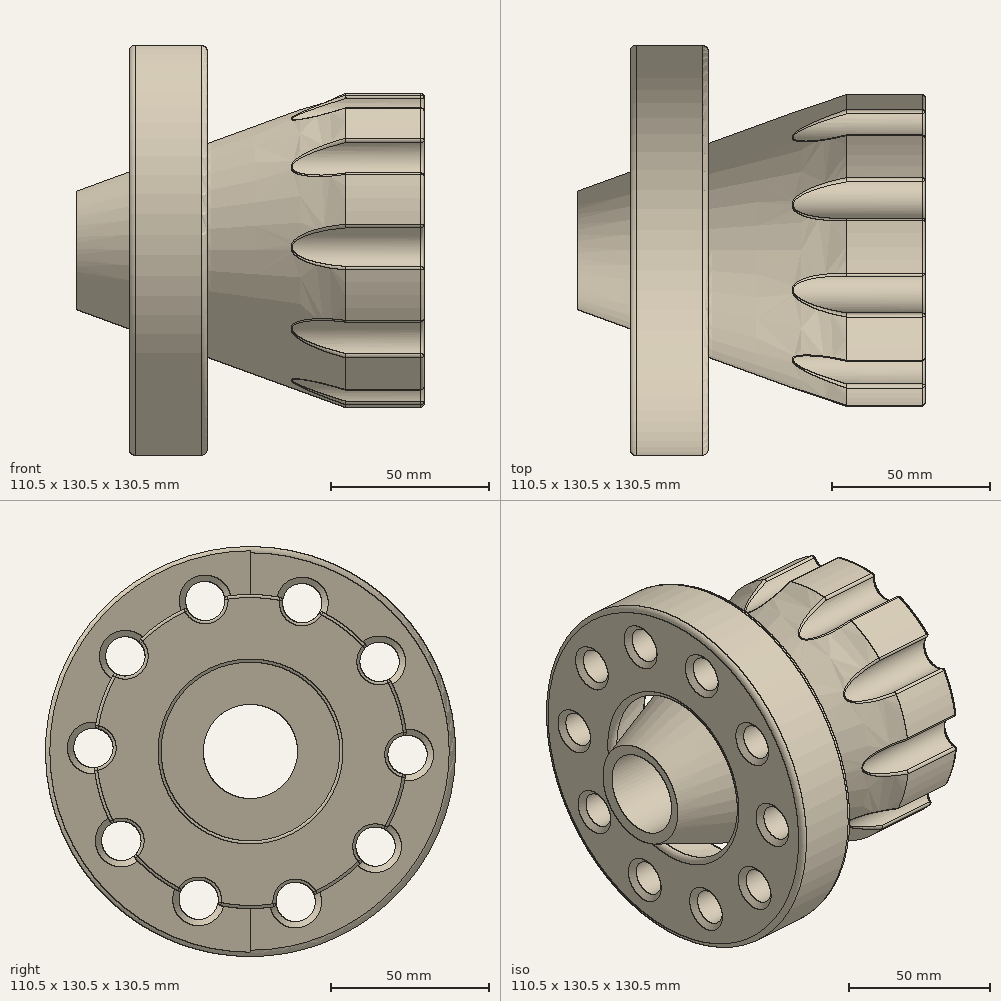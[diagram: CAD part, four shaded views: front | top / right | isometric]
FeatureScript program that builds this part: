
annotation { "Feature Type Name" : "Feature", "Feature Type Description" : "" }
export const myFeature = defineFeature(function(context is Context, id is Id, definition is map)
    precondition{}
    {
        {
            var Q0;
            Q0 = qCreatedBy(makeId("Front.planeOp"), FACE);
            var sketch = newSketch(context, id + "F0", { "sketchPlane" : qUnion([Q0])});
            skLineSegment(sketch, "E0", {"start": v(-83.1, 0) * mm, "end": v(0, 0) * mm, "construction": true});
            skLineSegment(sketch, "E1.bottom", {"start": v(25, 39.34) * mm, "end": v(0, 30.24) * mm});
            skLineSegment(sketch, "E1.top", {"start": v(25, 65.24) * mm, "end": v(0, 65.24) * mm});
            skLineSegment(sketch, "E1.left", {"start": v(25, 39.34) * mm, "end": v(25, 65.24) * mm});
            skLineSegment(sketch, "E1.right", {"start": v(0, 30.24) * mm, "end": v(0, 65.24) * mm});
            skLineSegment(sketch, "E2.0", {"start": v(68.9, 50) * mm, "end": v(-27.26, 15) * mm});
            skLineSegment(sketch, "E3", {"start": v(68.9, 50) * mm, "end": v(68.9, 15) * mm});
            skLineSegment(sketch, "E4", {"start": v(68.9, 15) * mm, "end": v(-27.26, 15) * mm});
            skPoint(sketch, "E5", {"position": v(-68.47, 0) * mm});
            skLineSegment(sketch, "E6", {"start": v(0, 0) * mm, "end": v(-68.47, 0) * mm});
            skSolve(sketch);
        }
        {
            var Q0;
            Q0=makeQuery(id+"F0.imprint","IMPRINT",FACE,{"disambiguationData":[TD([[makeQuery(id+"F0.imprint","IMPRINT",EDGE,{"derivedFrom":sQuery(id+"F0.wireOp",EDGE,"E2.0")}),1.0]])]});
            var Q1;
            Q1=sQuery(id+"F0.wireOp",EDGE,"E0");
            revolve(context, id + "F1", {"entities" : qUnion([Q0]), "axis" : qUnion([Q1]), "revolveType" : RevolveType.FULL});
        }
        {
            var Q0;
            Q0=makeQuery(id+"F1.opRevolve","SWEPT_FACE",FACE,{"disambiguationData":[OSD([sQuery(id+"F0.wireOp",EDGE,"E3")])]});
            var sketch = newSketch(context, id + "F2", { "sketchPlane" : qUnion([Q0])});
            skCircle(sketch, "E7", {"center": v(-49.99, 1.1) * mm, "radius": 6.26 * mm});
            skSolve(sketch);
        }
        {
            var Q0;
            {var subQ0=makeQuery(id+"F1.opRevolve","SWEPT_EDGE",EDGE,{"disambiguationData":[OSD([sQuery(id+"F0.wireOp",EDGE,"E2.0"),sQuery(id+"F0.wireOp",EDGE,"E3")])]});var subQ1=sQuery(id+"F2.wireOp",EDGE,"E7");var subQ3=makeQuery(id+"F2.imprint","INTERSECT",VERTEX,{"disambiguationData":[OD(0.0)],"derivedFrom":[subQ0,subQ1]});Q0=qUnion([makeQuery(id+"F2.imprint","IMPRINT",FACE,{"disambiguationData":[TD([[makeQuery(id+"F2.imprint","IMPRINT",EDGE,{"disambiguationData":[TD([[subQ3,1.0]])],"derivedFrom":subQ1}),1.0]])]}),makeQuery(id+"F2.imprint","IMPRINT",FACE,{"disambiguationData":[TD([[makeQuery(id+"F2.imprint","IMPRINT",EDGE,{"disambiguationData":[TD([[subQ3,-1.0]])],"derivedFrom":subQ1}),1.0]])]})]);}
            extrude(context, id + "F3", {"entities" : qUnion([Q0]), "oppositeDirection" : true, "depth" : 131.33 * mm});
        }
        {
            var Q0;
            Q0=makeQuery(id+"F3.opExtrude","SWEPT_BODY",BODY,{"disambiguationData":[OSD([sQuery(id+"F2.wireOp",EDGE,"E7")])]});
            var Q1;
            Q1=makeQuery(id+"F1.opRevolve","SWEPT_FACE",FACE,{"disambiguationData":[OSD([sQuery(id+"F0.wireOp",EDGE,"E4")])]});
            circularPattern(context, id + "F4", {"entities" : qUnion([Q0]), "axis" : qUnion([Q1]), "angle" : 360 * degree, "instanceCount" : 10, "equalSpace" : true});
        }
        {
            var Q0;
            Q0=makeQuery(id+"F0.imprint","IMPRINT",FACE,{"disambiguationData":[TD([[makeQuery(id+"F0.imprint","IMPRINT",EDGE,{"derivedFrom":sQuery(id+"F0.wireOp",EDGE,"E1.bottom")}),-1.0]])]});
            var Q1;
            Q1=sQuery(id+"F0.wireOp",EDGE,"E0");
            revolve(context, id + "F5", {"entities" : qUnion([Q0]), "axis" : qUnion([Q1]), "revolveType" : RevolveType.FULL});
        }
        {
            var Q0;
            Q0=makeQuery(id+"F4.opPattern","COPY",BODY,{"derivedFrom":makeQuery(id+"F3.opExtrude","SWEPT_BODY",BODY,{"disambiguationData":[OSD([sQuery(id+"F2.wireOp",EDGE,"E7")])]}),"instanceName":"4"});
            var Q1;
            Q1=makeQuery(id+"F4.opPattern","COPY",BODY,{"derivedFrom":makeQuery(id+"F3.opExtrude","SWEPT_BODY",BODY,{"disambiguationData":[OSD([sQuery(id+"F2.wireOp",EDGE,"E7")])]}),"instanceName":"3"});
            var Q2;
            Q2=makeQuery(id+"F4.opPattern","COPY",BODY,{"derivedFrom":makeQuery(id+"F3.opExtrude","SWEPT_BODY",BODY,{"disambiguationData":[OSD([sQuery(id+"F2.wireOp",EDGE,"E7")])]}),"instanceName":"2"});
            var Q3;
            Q3=makeQuery(id+"F4.opPattern","COPY",BODY,{"derivedFrom":makeQuery(id+"F3.opExtrude","SWEPT_BODY",BODY,{"disambiguationData":[OSD([sQuery(id+"F2.wireOp",EDGE,"E7")])]}),"instanceName":"1"});
            var Q4;
            Q4=makeQuery(id+"F3.opExtrude","SWEPT_BODY",BODY,{"disambiguationData":[OSD([sQuery(id+"F2.wireOp",EDGE,"E7")])]});
            var Q5;
            Q5=makeQuery(id+"F4.opPattern","COPY",BODY,{"derivedFrom":makeQuery(id+"F3.opExtrude","SWEPT_BODY",BODY,{"disambiguationData":[OSD([sQuery(id+"F2.wireOp",EDGE,"E7")])]}),"instanceName":"9"});
            var Q6;
            Q6=makeQuery(id+"F4.opPattern","COPY",BODY,{"derivedFrom":makeQuery(id+"F3.opExtrude","SWEPT_BODY",BODY,{"disambiguationData":[OSD([sQuery(id+"F2.wireOp",EDGE,"E7")])]}),"instanceName":"8"});
            var Q7;
            Q7=makeQuery(id+"F4.opPattern","COPY",BODY,{"derivedFrom":makeQuery(id+"F3.opExtrude","SWEPT_BODY",BODY,{"disambiguationData":[OSD([sQuery(id+"F2.wireOp",EDGE,"E7")])]}),"instanceName":"7"});
            var Q8;
            Q8=makeQuery(id+"F4.opPattern","COPY",BODY,{"derivedFrom":makeQuery(id+"F3.opExtrude","SWEPT_BODY",BODY,{"disambiguationData":[OSD([sQuery(id+"F2.wireOp",EDGE,"E7")])]}),"instanceName":"6"});
            var Q9;
            Q9=makeQuery(id+"F4.opPattern","COPY",BODY,{"derivedFrom":makeQuery(id+"F3.opExtrude","SWEPT_BODY",BODY,{"disambiguationData":[OSD([sQuery(id+"F2.wireOp",EDGE,"E7")])]}),"instanceName":"5"});
            var Q10;
            Q10=makeQuery(id+"F1.opRevolve","SWEPT_BODY",BODY,{"disambiguationData":[OSD([sQuery(id+"F0.wireOp",EDGE,"E2.0"),sQuery(id+"F0.wireOp",EDGE,"E3"),sQuery(id+"F0.wireOp",EDGE,"E4")])]});
            var Q11;
            Q11=makeQuery(id+"F5.opRevolve","SWEPT_BODY",BODY,{"disambiguationData":[OSD([sQuery(id+"F0.wireOp",EDGE,"E1.bottom"),sQuery(id+"F0.wireOp",EDGE,"E1.top"),sQuery(id+"F0.wireOp",EDGE,"E1.left"),sQuery(id+"F0.wireOp",EDGE,"E1.right")])]});
            booleanBodies(context, id + "F6", {"operationType" : BooleanOperationType.SUBTRACTION, "tools" : qUnion([Q0, Q1, Q2, Q3, Q4, Q5, Q6, Q7, Q8, Q9]), "targets" : qUnion([Q10, Q11])});
        }
        {
            var Q0;
            Q0=makeQuery(id+"F1.opRevolve","SWEPT_FACE",FACE,{"disambiguationData":[OSD([sQuery(id+"F0.wireOp",EDGE,"E3")])]});
            extrude(context, id + "F7", {"entities" : qUnion([Q0]), "operationType" : NewBodyOperationType.ADD, "depth" : 25 * mm});
        }
        {
            var Q0;
            Q0=makeQuery(id+"F5.opRevolve","SWEPT_FACE",FACE,{"disambiguationData":[OSD([sQuery(id+"F0.wireOp",EDGE,"E1.left")])]});
            var sketch = newSketch(context, id + "F8", { "sketchPlane" : qUnion([Q0])});
            skLineSegment(sketch, "E8.bottom", {"start": v(-102.18, 110.86) * mm, "end": v(0, 110.86) * mm});
            skLineSegment(sketch, "E8.top", {"start": v(-102.18, -86.82) * mm, "end": v(0, -86.82) * mm});
            skLineSegment(sketch, "E8.left", {"start": v(-102.18, 110.86) * mm, "end": v(-102.18, -86.82) * mm});
            skLineSegment(sketch, "E8.right", {"start": v(0, 110.86) * mm, "end": v(0, -86.82) * mm});
            skSolve(sketch);
        }
        {
            var Q0;
            {var subQ0=makeQuery(id+"F3.opExtrude","SWEPT_FACE",FACE,{"disambiguationData":[OSD([sQuery(id+"F2.wireOp",EDGE,"E7")])]});var subQ1=sQuery(id+"F0.wireOp",EDGE,"E1.left");var subQ2=makeQuery(id+"F5.opRevolve","SWEPT_FACE",FACE,{"disambiguationData":[OSD([subQ1])]});var subQ3=makeQuery(id+"F8.imprint","IMPRINT",EDGE,{"derivedFrom":makeQuery(id+"F6.opBoolean","INTERSECT",EDGE,{"derivedFrom":[subQ0,subQ2]})});var subQ4=makeQuery(id+"F8.imprint","IMPRINT",EDGE,{"derivedFrom":makeQuery(id+"F6.opBoolean","INTERSECT",EDGE,{"derivedFrom":[makeQuery(id+"F4.opPattern","COPY",FACE,{"derivedFrom":subQ0,"instanceName":"1"}),subQ2]})});var subQ5=makeQuery(id+"F8.imprint","IMPRINT",EDGE,{"derivedFrom":makeQuery(id+"F6.opBoolean","INTERSECT",EDGE,{"derivedFrom":[makeQuery(id+"F4.opPattern","COPY",FACE,{"derivedFrom":subQ0,"instanceName":"2"}),subQ2]})});var subQ6=makeQuery(id+"F8.imprint","IMPRINT",EDGE,{"derivedFrom":makeQuery(id+"F6.opBoolean","INTERSECT",EDGE,{"derivedFrom":[makeQuery(id+"F4.opPattern","COPY",FACE,{"derivedFrom":subQ0,"instanceName":"8"}),subQ2]})});var subQ7=makeQuery(id+"F8.imprint","IMPRINT",EDGE,{"derivedFrom":makeQuery(id+"F6.opBoolean","INTERSECT",EDGE,{"derivedFrom":[makeQuery(id+"F4.opPattern","COPY",FACE,{"derivedFrom":subQ0,"instanceName":"9"}),subQ2]})});var subQ9=sQuery(id+"F8.wireOp",EDGE,"E8.right");var subQ14=sQuery(id+"F8.wireOp",EDGE,"E8.bottom");var subQ15=makeQuery(id+"F5.opRevolve","SWEPT_EDGE",EDGE,{"disambiguationData":[OSD([sQuery(id+"F0.wireOp",EDGE,"E1.bottom"),subQ1])]});var subQ17=makeQuery(id+"F8.imprint","INTERSECT",VERTEX,{"disambiguationData":[OD(0.0)],"derivedFrom":[subQ15,subQ9]});Q0=qUnion([makeQuery(id+"F8.imprint","IMPRINT",FACE,{"disambiguationData":[TD([[subQ3,-1.0]])]}),makeQuery(id+"F8.imprint","IMPRINT",FACE,{"disambiguationData":[TD([[subQ4,-1.0]])]}),makeQuery(id+"F8.imprint","IMPRINT",FACE,{"disambiguationData":[TD([[subQ5,-1.0]])]}),makeQuery(id+"F8.imprint","IMPRINT",FACE,{"disambiguationData":[TD([[subQ6,-1.0]])]}),makeQuery(id+"F8.imprint","IMPRINT",FACE,{"disambiguationData":[TD([[subQ7,-1.0]])]}),makeQuery(id+"F8.imprint","IMPRINT",FACE,{"disambiguationData":[TD([[makeQuery(id+"F8.imprint","IMPRINT",EDGE,{"derivedFrom":subQ14}),-1.0]])]}),makeQuery(id+"F8.imprint","IMPRINT",FACE,{"disambiguationData":[TD([[subQ3,1.0]])]}),makeQuery(id+"F8.imprint","IMPRINT",FACE,{"disambiguationData":[TD([[makeQuery(id+"F8.imprint","IMPRINT",EDGE,{"disambiguationData":[TD([[subQ17,-1.0]])],"derivedFrom":subQ9}),-1.0]])]})]);}
            extrude(context, id + "F9", {"entities" : qUnion([Q0]), "operationType" : NewBodyOperationType.REMOVE, "oppositeDirection" : true, "depth" : .1 * mm});
        }
        {
            var Q0;
            Q0=makeQuery(id+"F5.opRevolve","SWEPT_EDGE",EDGE,{"disambiguationData":[OSD([sQuery(id+"F0.wireOp",EDGE,"E1.bottom"),sQuery(id+"F0.wireOp",EDGE,"E1.left")])]});
            var Q1;
            Q1=makeQuery(id+"F5.opRevolve","SWEPT_EDGE",EDGE,{"disambiguationData":[OSD([sQuery(id+"F0.wireOp",EDGE,"E1.top"),sQuery(id+"F0.wireOp",EDGE,"E1.left")])]});
            var Q2;
            Q2=makeQuery(id+"F5.opRevolve","SWEPT_EDGE",EDGE,{"disambiguationData":[OSD([sQuery(id+"F0.wireOp",EDGE,"E1.top"),sQuery(id+"F0.wireOp",EDGE,"E1.right")])]});
            var Q3;
            Q3=makeQuery(id+"F5.opRevolve","SWEPT_EDGE",EDGE,{"disambiguationData":[OSD([sQuery(id+"F0.wireOp",EDGE,"E1.bottom"),sQuery(id+"F0.wireOp",EDGE,"E1.right")])]});
            fillet(context, id + "F10", {"entities" : qUnion([Q0, Q1, Q2, Q3]), "radius" : 2 * mm, "tangentPropagation" : true, "allowEdgeOverflow" : false});
        }
        {
            var Q0;
            Q0=makeQuery(id+"F5.opRevolve","SWEPT_FACE",FACE,{"disambiguationData":[OSD([sQuery(id+"F0.wireOp",EDGE,"E1.right")])]});
            var Q1;
            Q1=makeQuery(id+"F1.opRevolve","SWEPT_EDGE",EDGE,{"disambiguationData":[OSD([sQuery(id+"F0.wireOp",EDGE,"E2.0"),sQuery(id+"F0.wireOp",EDGE,"E4")])]});
            var Q2;
            Q2=makeQuery(id+"F6.opBoolean","INTERSECT",EDGE,{"derivedFrom":[makeQuery(id+"F4.opPattern","COPY",FACE,{"derivedFrom":makeQuery(id+"F3.opExtrude","SWEPT_FACE",FACE,{"disambiguationData":[OSD([sQuery(id+"F2.wireOp",EDGE,"E7")])]}),"instanceName":"3"}),makeQuery(id+"F5.opRevolve","SWEPT_FACE",FACE,{"disambiguationData":[OSD([sQuery(id+"F0.wireOp",EDGE,"E1.left")])]})]});
            var Q3;
            Q3=makeQuery(id+"F9.boolean.opBoolean","INTERSECT",EDGE,{"derivedFrom":[makeQuery(id+"F6.opBoolean","COPY",FACE,{"disambiguationData":[OD(1.0)],"derivedFrom":makeQuery(id+"F4.opPattern","COPY",FACE,{"derivedFrom":makeQuery(id+"F3.opExtrude","SWEPT_FACE",FACE,{"disambiguationData":[OSD([sQuery(id+"F2.wireOp",EDGE,"E7")])]}),"instanceName":"2"})}),makeQuery(id+"F9.opExtrude","CAP_FACE",FACE,{"disambiguationData":[OSD([sQuery(id+"F8.wireOp",EDGE,"E8.bottom"),sQuery(id+"F8.wireOp",EDGE,"E8.top"),sQuery(id+"F8.wireOp",EDGE,"E8.left"),sQuery(id+"F8.wireOp",EDGE,"E8.right")])],"isStart":false})]});
            var Q4;
            Q4=makeQuery(id+"F9.boolean.opBoolean","INTERSECT",EDGE,{"derivedFrom":[makeQuery(id+"F6.opBoolean","COPY",FACE,{"disambiguationData":[OD(1.0)],"derivedFrom":makeQuery(id+"F4.opPattern","COPY",FACE,{"derivedFrom":makeQuery(id+"F3.opExtrude","SWEPT_FACE",FACE,{"disambiguationData":[OSD([sQuery(id+"F2.wireOp",EDGE,"E7")])]}),"instanceName":"1"})}),makeQuery(id+"F9.opExtrude","CAP_FACE",FACE,{"disambiguationData":[OSD([sQuery(id+"F8.wireOp",EDGE,"E8.bottom"),sQuery(id+"F8.wireOp",EDGE,"E8.top"),sQuery(id+"F8.wireOp",EDGE,"E8.left"),sQuery(id+"F8.wireOp",EDGE,"E8.right")])],"isStart":false})]});
            var Q5;
            Q5=makeQuery(id+"F9.boolean.opBoolean","INTERSECT",EDGE,{"derivedFrom":[makeQuery(id+"F6.opBoolean","COPY",FACE,{"disambiguationData":[OD(1.0)],"derivedFrom":makeQuery(id+"F3.opExtrude","SWEPT_FACE",FACE,{"disambiguationData":[OSD([sQuery(id+"F2.wireOp",EDGE,"E7")])]})}),makeQuery(id+"F9.opExtrude","CAP_FACE",FACE,{"disambiguationData":[OSD([sQuery(id+"F8.wireOp",EDGE,"E8.bottom"),sQuery(id+"F8.wireOp",EDGE,"E8.top"),sQuery(id+"F8.wireOp",EDGE,"E8.left"),sQuery(id+"F8.wireOp",EDGE,"E8.right")])],"isStart":false})]});
            var Q6;
            Q6=makeQuery(id+"F9.boolean.opBoolean","INTERSECT",EDGE,{"derivedFrom":[makeQuery(id+"F6.opBoolean","COPY",FACE,{"disambiguationData":[OD(1.0)],"derivedFrom":makeQuery(id+"F4.opPattern","COPY",FACE,{"derivedFrom":makeQuery(id+"F3.opExtrude","SWEPT_FACE",FACE,{"disambiguationData":[OSD([sQuery(id+"F2.wireOp",EDGE,"E7")])]}),"instanceName":"9"})}),makeQuery(id+"F9.opExtrude","CAP_FACE",FACE,{"disambiguationData":[OSD([sQuery(id+"F8.wireOp",EDGE,"E8.bottom"),sQuery(id+"F8.wireOp",EDGE,"E8.top"),sQuery(id+"F8.wireOp",EDGE,"E8.left"),sQuery(id+"F8.wireOp",EDGE,"E8.right")])],"isStart":false})]});
            var Q7;
            Q7=makeQuery(id+"F9.boolean.opBoolean","INTERSECT",EDGE,{"derivedFrom":[makeQuery(id+"F6.opBoolean","COPY",FACE,{"disambiguationData":[OD(1.0)],"derivedFrom":makeQuery(id+"F4.opPattern","COPY",FACE,{"derivedFrom":makeQuery(id+"F3.opExtrude","SWEPT_FACE",FACE,{"disambiguationData":[OSD([sQuery(id+"F2.wireOp",EDGE,"E7")])]}),"instanceName":"8"})}),makeQuery(id+"F9.opExtrude","CAP_FACE",FACE,{"disambiguationData":[OSD([sQuery(id+"F8.wireOp",EDGE,"E8.bottom"),sQuery(id+"F8.wireOp",EDGE,"E8.top"),sQuery(id+"F8.wireOp",EDGE,"E8.left"),sQuery(id+"F8.wireOp",EDGE,"E8.right")])],"isStart":false})]});
            var Q8;
            Q8=makeQuery(id+"F6.opBoolean","INTERSECT",EDGE,{"derivedFrom":[makeQuery(id+"F4.opPattern","COPY",FACE,{"derivedFrom":makeQuery(id+"F3.opExtrude","SWEPT_FACE",FACE,{"disambiguationData":[OSD([sQuery(id+"F2.wireOp",EDGE,"E7")])]}),"instanceName":"7"}),makeQuery(id+"F5.opRevolve","SWEPT_FACE",FACE,{"disambiguationData":[OSD([sQuery(id+"F0.wireOp",EDGE,"E1.left")])]})]});
            var Q9;
            Q9=makeQuery(id+"F6.opBoolean","INTERSECT",EDGE,{"derivedFrom":[makeQuery(id+"F4.opPattern","COPY",FACE,{"derivedFrom":makeQuery(id+"F3.opExtrude","SWEPT_FACE",FACE,{"disambiguationData":[OSD([sQuery(id+"F2.wireOp",EDGE,"E7")])]}),"instanceName":"6"}),makeQuery(id+"F5.opRevolve","SWEPT_FACE",FACE,{"disambiguationData":[OSD([sQuery(id+"F0.wireOp",EDGE,"E1.left")])]})]});
            var Q10;
            Q10=makeQuery(id+"F6.opBoolean","INTERSECT",EDGE,{"derivedFrom":[makeQuery(id+"F4.opPattern","COPY",FACE,{"derivedFrom":makeQuery(id+"F3.opExtrude","SWEPT_FACE",FACE,{"disambiguationData":[OSD([sQuery(id+"F2.wireOp",EDGE,"E7")])]}),"instanceName":"5"}),makeQuery(id+"F5.opRevolve","SWEPT_FACE",FACE,{"disambiguationData":[OSD([sQuery(id+"F0.wireOp",EDGE,"E1.left")])]})]});
            var Q11;
            Q11=makeQuery(id+"F6.opBoolean","INTERSECT",EDGE,{"derivedFrom":[makeQuery(id+"F4.opPattern","COPY",FACE,{"derivedFrom":makeQuery(id+"F3.opExtrude","SWEPT_FACE",FACE,{"disambiguationData":[OSD([sQuery(id+"F2.wireOp",EDGE,"E7")])]}),"instanceName":"4"}),makeQuery(id+"F5.opRevolve","SWEPT_FACE",FACE,{"disambiguationData":[OSD([sQuery(id+"F0.wireOp",EDGE,"E1.left")])]})]});
            chamfer(context, id + "F11", {"entities" : qUnion([Q0, Q1, Q2, Q3, Q4, Q5, Q6, Q7, Q8, Q9, Q10, Q11]), "width" : 2 * mm, "tangentPropagation" : true});
        }
        {
            var Q0;
            Q0=makeQuery(id+"F7.opExtrude","CAP_FACE",FACE,{"disambiguationData":[OSD([sQuery(id+"F0.wireOp",EDGE,"E3")])],"isStart":false});
            var sketch = newSketch(context, id + "F12", { "sketchPlane" : qUnion([Q0])});
            skCircle(sketch, "E9", {"center": v(0, 0) * mm, "radius": 28.42 * mm});
            skSolve(sketch);
        }
        {
            var Q0;
            {var subQ0=makeQuery(id+"F12.imprint","IMPRINT",EDGE,{"derivedFrom":makeQuery(id+"F7.opExtrude","CAP_EDGE",EDGE,{"disambiguationData":[OSD([sQuery(id+"F0.wireOp",EDGE,"E3"),sQuery(id+"F0.wireOp",EDGE,"E4")])],"isStart":false})});Q0=qUnion([makeQuery(id+"F12.imprint","IMPRINT",FACE,{"disambiguationData":[TD([[subQ0,-1.0]])]}),makeQuery(id+"F12.imprint","IMPRINT",FACE,{"disambiguationData":[TD([[makeQuery(id+"F12.imprint","IMPRINT",EDGE,{"derivedFrom":sQuery(id+"F12.wireOp",EDGE,"E9")}),1.0]])]})]);}
            extrude(context, id + "F13", {"entities" : qUnion([Q0]), "operationType" : NewBodyOperationType.REMOVE, "oppositeDirection" : true, "depth" : 37.2 * mm});
        }
        {
            var Q0;
            {var subQ0=sQuery(id+"F2.wireOp",EDGE,"E7");Q0=makeQuery(id+"F7.boolean.opBoolean","MERGE",FACE,{"derivedFrom":[makeQuery(id+"F6.opBoolean","COPY",FACE,{"disambiguationData":[OD(0.0)],"derivedFrom":makeQuery(id+"F4.opPattern","COPY",FACE,{"derivedFrom":makeQuery(id+"F3.opExtrude","SWEPT_FACE",FACE,{"disambiguationData":[OSD([subQ0])]}),"instanceName":"4"})}),makeQuery(id+"F7.opExtrude","SWEPT_FACE",FACE,{"disambiguationData":[OSD([subQ0]),TDD([makeQuery(id+"F6.opBoolean","COPY",EDGE,{"derivedFrom":makeQuery(id+"F4.opPattern","COPY",EDGE,{"derivedFrom":makeQuery(id+"F3.opExtrude","CAP_EDGE",EDGE,{"disambiguationData":[OSD([subQ0])],"isStart":true}),"instanceName":"4"})})])]})]});}
            var Q1;
            {var subQ0=sQuery(id+"F2.wireOp",EDGE,"E7");Q1=makeQuery(id+"F7.boolean.opBoolean","MERGE",FACE,{"derivedFrom":[makeQuery(id+"F6.opBoolean","COPY",FACE,{"disambiguationData":[OD(0.0)],"derivedFrom":makeQuery(id+"F4.opPattern","COPY",FACE,{"derivedFrom":makeQuery(id+"F3.opExtrude","SWEPT_FACE",FACE,{"disambiguationData":[OSD([subQ0])]}),"instanceName":"3"})}),makeQuery(id+"F7.opExtrude","SWEPT_FACE",FACE,{"disambiguationData":[OSD([subQ0]),TDD([makeQuery(id+"F6.opBoolean","COPY",EDGE,{"derivedFrom":makeQuery(id+"F4.opPattern","COPY",EDGE,{"derivedFrom":makeQuery(id+"F3.opExtrude","CAP_EDGE",EDGE,{"disambiguationData":[OSD([subQ0])],"isStart":true}),"instanceName":"3"})})])]})]});}
            var Q2;
            {var subQ0=sQuery(id+"F2.wireOp",EDGE,"E7");Q2=makeQuery(id+"F7.boolean.opBoolean","MERGE",FACE,{"derivedFrom":[makeQuery(id+"F6.opBoolean","COPY",FACE,{"disambiguationData":[OD(0.0)],"derivedFrom":makeQuery(id+"F4.opPattern","COPY",FACE,{"derivedFrom":makeQuery(id+"F3.opExtrude","SWEPT_FACE",FACE,{"disambiguationData":[OSD([subQ0])]}),"instanceName":"5"})}),makeQuery(id+"F7.opExtrude","SWEPT_FACE",FACE,{"disambiguationData":[OSD([subQ0]),TDD([makeQuery(id+"F6.opBoolean","COPY",EDGE,{"derivedFrom":makeQuery(id+"F4.opPattern","COPY",EDGE,{"derivedFrom":makeQuery(id+"F3.opExtrude","CAP_EDGE",EDGE,{"disambiguationData":[OSD([subQ0])],"isStart":true}),"instanceName":"5"})})])]})]});}
            var Q3;
            {var subQ0=sQuery(id+"F2.wireOp",EDGE,"E7");Q3=makeQuery(id+"F7.boolean.opBoolean","MERGE",FACE,{"derivedFrom":[makeQuery(id+"F6.opBoolean","COPY",FACE,{"disambiguationData":[OD(0.0)],"derivedFrom":makeQuery(id+"F4.opPattern","COPY",FACE,{"derivedFrom":makeQuery(id+"F3.opExtrude","SWEPT_FACE",FACE,{"disambiguationData":[OSD([subQ0])]}),"instanceName":"6"})}),makeQuery(id+"F7.opExtrude","SWEPT_FACE",FACE,{"disambiguationData":[OSD([subQ0]),TDD([makeQuery(id+"F6.opBoolean","COPY",EDGE,{"derivedFrom":makeQuery(id+"F4.opPattern","COPY",EDGE,{"derivedFrom":makeQuery(id+"F3.opExtrude","CAP_EDGE",EDGE,{"disambiguationData":[OSD([subQ0])],"isStart":true}),"instanceName":"6"})})])]})]});}
            var Q4;
            {var subQ0=sQuery(id+"F2.wireOp",EDGE,"E7");Q4=makeQuery(id+"F7.boolean.opBoolean","MERGE",FACE,{"derivedFrom":[makeQuery(id+"F6.opBoolean","COPY",FACE,{"disambiguationData":[OD(0.0)],"derivedFrom":makeQuery(id+"F4.opPattern","COPY",FACE,{"derivedFrom":makeQuery(id+"F3.opExtrude","SWEPT_FACE",FACE,{"disambiguationData":[OSD([subQ0])]}),"instanceName":"7"})}),makeQuery(id+"F7.opExtrude","SWEPT_FACE",FACE,{"disambiguationData":[OSD([subQ0]),TDD([makeQuery(id+"F6.opBoolean","COPY",EDGE,{"derivedFrom":makeQuery(id+"F4.opPattern","COPY",EDGE,{"derivedFrom":makeQuery(id+"F3.opExtrude","CAP_EDGE",EDGE,{"disambiguationData":[OSD([subQ0])],"isStart":true}),"instanceName":"7"})})])]})]});}
            var Q5;
            {var subQ0=sQuery(id+"F2.wireOp",EDGE,"E7");Q5=makeQuery(id+"F7.boolean.opBoolean","MERGE",FACE,{"derivedFrom":[makeQuery(id+"F6.opBoolean","COPY",FACE,{"disambiguationData":[OD(0.0)],"derivedFrom":makeQuery(id+"F4.opPattern","COPY",FACE,{"derivedFrom":makeQuery(id+"F3.opExtrude","SWEPT_FACE",FACE,{"disambiguationData":[OSD([subQ0])]}),"instanceName":"8"})}),makeQuery(id+"F7.opExtrude","SWEPT_FACE",FACE,{"disambiguationData":[OSD([subQ0]),TDD([makeQuery(id+"F6.opBoolean","COPY",EDGE,{"derivedFrom":makeQuery(id+"F4.opPattern","COPY",EDGE,{"derivedFrom":makeQuery(id+"F3.opExtrude","CAP_EDGE",EDGE,{"disambiguationData":[OSD([subQ0])],"isStart":true}),"instanceName":"8"})})])]})]});}
            var Q6;
            {var subQ0=sQuery(id+"F2.wireOp",EDGE,"E7");Q6=makeQuery(id+"F7.boolean.opBoolean","MERGE",FACE,{"derivedFrom":[makeQuery(id+"F6.opBoolean","COPY",FACE,{"disambiguationData":[OD(0.0)],"derivedFrom":makeQuery(id+"F4.opPattern","COPY",FACE,{"derivedFrom":makeQuery(id+"F3.opExtrude","SWEPT_FACE",FACE,{"disambiguationData":[OSD([subQ0])]}),"instanceName":"9"})}),makeQuery(id+"F7.opExtrude","SWEPT_FACE",FACE,{"disambiguationData":[OSD([subQ0]),TDD([makeQuery(id+"F6.opBoolean","COPY",EDGE,{"derivedFrom":makeQuery(id+"F4.opPattern","COPY",EDGE,{"derivedFrom":makeQuery(id+"F3.opExtrude","CAP_EDGE",EDGE,{"disambiguationData":[OSD([subQ0])],"isStart":true}),"instanceName":"9"})})])]})]});}
            var Q7;
            {var subQ0=sQuery(id+"F2.wireOp",EDGE,"E7");Q7=makeQuery(id+"F7.boolean.opBoolean","MERGE",FACE,{"derivedFrom":[makeQuery(id+"F6.opBoolean","COPY",FACE,{"disambiguationData":[OD(0.0)],"derivedFrom":makeQuery(id+"F3.opExtrude","SWEPT_FACE",FACE,{"disambiguationData":[OSD([subQ0])]})}),makeQuery(id+"F7.opExtrude","SWEPT_FACE",FACE,{"disambiguationData":[OSD([subQ0]),TDD([makeQuery(id+"F6.opBoolean","COPY",EDGE,{"derivedFrom":makeQuery(id+"F3.opExtrude","CAP_EDGE",EDGE,{"disambiguationData":[OSD([subQ0])],"isStart":true})})])]})]});}
            var Q8;
            {var subQ0=sQuery(id+"F2.wireOp",EDGE,"E7");Q8=makeQuery(id+"F7.boolean.opBoolean","MERGE",FACE,{"derivedFrom":[makeQuery(id+"F6.opBoolean","COPY",FACE,{"disambiguationData":[OD(0.0)],"derivedFrom":makeQuery(id+"F4.opPattern","COPY",FACE,{"derivedFrom":makeQuery(id+"F3.opExtrude","SWEPT_FACE",FACE,{"disambiguationData":[OSD([subQ0])]}),"instanceName":"1"})}),makeQuery(id+"F7.opExtrude","SWEPT_FACE",FACE,{"disambiguationData":[OSD([subQ0]),TDD([makeQuery(id+"F6.opBoolean","COPY",EDGE,{"derivedFrom":makeQuery(id+"F4.opPattern","COPY",EDGE,{"derivedFrom":makeQuery(id+"F3.opExtrude","CAP_EDGE",EDGE,{"disambiguationData":[OSD([subQ0])],"isStart":true}),"instanceName":"1"})})])]})]});}
            var Q9;
            Q9=makeQuery(id+"F1.opRevolve","SWEPT_FACE",FACE,{"disambiguationData":[OSD([sQuery(id+"F0.wireOp",EDGE,"E3")])]});
            var Q10;
            {var subQ0=sQuery(id+"F2.wireOp",EDGE,"E7");Q10=makeQuery(id+"F7.boolean.opBoolean","MERGE",FACE,{"derivedFrom":[makeQuery(id+"F6.opBoolean","COPY",FACE,{"disambiguationData":[OD(0.0)],"derivedFrom":makeQuery(id+"F4.opPattern","COPY",FACE,{"derivedFrom":makeQuery(id+"F3.opExtrude","SWEPT_FACE",FACE,{"disambiguationData":[OSD([subQ0])]}),"instanceName":"2"})}),makeQuery(id+"F7.opExtrude","SWEPT_FACE",FACE,{"disambiguationData":[OSD([subQ0]),TDD([makeQuery(id+"F6.opBoolean","COPY",EDGE,{"derivedFrom":makeQuery(id+"F4.opPattern","COPY",EDGE,{"derivedFrom":makeQuery(id+"F3.opExtrude","CAP_EDGE",EDGE,{"disambiguationData":[OSD([subQ0])],"isStart":true}),"instanceName":"2"})})])]})]});}
            var Q11;
            Q11=makeQuery(id+"F7.opExtrude","CAP_FACE",FACE,{"disambiguationData":[OSD([sQuery(id+"F0.wireOp",EDGE,"E3")])],"isStart":false});
            fillet(context, id + "F14", {"entities" : qUnion([Q0, Q1, Q2, Q3, Q4, Q5, Q6, Q7, Q8, Q9, Q10, Q11]), "radius" : 1 * mm, "tangentPropagation" : true, "allowEdgeOverflow" : false});
        }
    });
